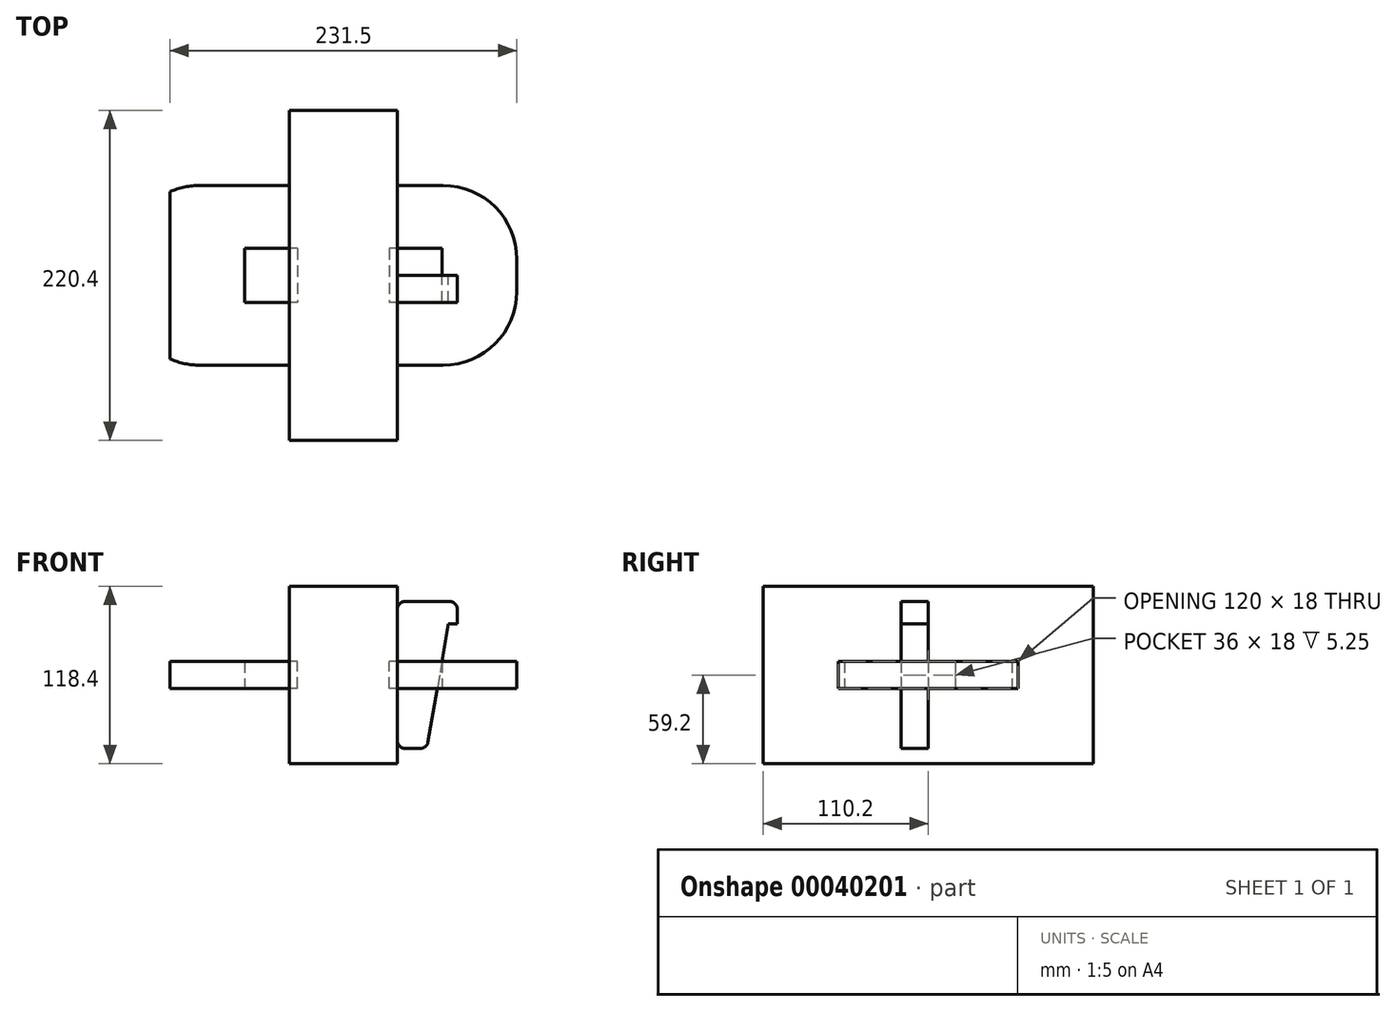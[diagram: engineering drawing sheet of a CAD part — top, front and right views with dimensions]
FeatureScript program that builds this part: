
annotation { "Feature Type Name" : "Feature", "Feature Type Description" : "" }
export const myFeature = defineFeature(function(context is Context, id is Id, definition is map)
    precondition{}
    {
        {
            var Q0;
            Q0=qCreatedBy(makeId("Top.planeOp"),FACE);
            var sketch = newSketch(context, id + "F0", { "sketchPlane" : qUnion([Q0])});
            skLineSegment(sketch, "E0.rect.bottom", {"start": v(95.75, -60) * mm, "end": v(-95.75, -60) * mm});
            skLineSegment(sketch, "E0.rect.top", {"start": v(95.75, 60) * mm, "end": v(-95.75, 60) * mm});
            skLineSegment(sketch, "E0.rect.left", {"start": v(145.75, -10) * mm, "end": v(145.75, 10) * mm});
            skLineSegment(sketch, "E0.rect.right", {"start": v(-145.75, -10) * mm, "end": v(-145.75, 10) * mm});
            skPoint(sketch, "E0.rect.middle", {"position": v(0, 0) * mm});
            skLineSegment(sketch, "E1.rect.bottom", {"start": v(65.75, -18) * mm, "end": v(-65.75, -18) * mm});
            skLineSegment(sketch, "E1.rect.top", {"start": v(65.75, 18) * mm, "end": v(-65.75, 18) * mm});
            skLineSegment(sketch, "E1.rect.left", {"start": v(65.75, -18) * mm, "end": v(65.75, 18) * mm});
            skLineSegment(sketch, "E1.rect.right", {"start": v(-65.75, -18) * mm, "end": v(-65.75, 18) * mm});
            skLineSegment(sketch, "E2", {"start": v(0, 0) * mm, "end": v(0, 60) * mm, "construction": true});
            skLineSegment(sketch, "E3", {"start": v(0, 0) * mm, "end": v(-24.77, 0) * mm, "construction": true});
            skPoint(sketch, "E4.visualSharp", {"position": v(-145.75, 60) * mm});
            skArc(sketch, "E4.filletArc", {"start": v(-95.75, 60) * mm, "mid": v(-131.1, 45.36) * mm, "end": v(-145.75, 10) * mm});
            skPoint(sketch, "E5.visualSharp", {"position": v(-145.75, -60) * mm});
            skArc(sketch, "E5.filletArc", {"start": v(-145.75, -10) * mm, "mid": v(-131.1, -45.36) * mm, "end": v(-95.75, -60) * mm});
            skPoint(sketch, "E6.visualSharp", {"position": v(145.75, 60) * mm});
            skArc(sketch, "E6.filletArc", {"start": v(145.75, 10) * mm, "mid": v(131.1, 45.36) * mm, "end": v(95.75, 60) * mm});
            skPoint(sketch, "E7.visualSharp", {"position": v(145.75, -60) * mm});
            skArc(sketch, "E7.filletArc", {"start": v(95.75, -60) * mm, "mid": v(131.1, -45.36) * mm, "end": v(145.75, -10) * mm});
            skSolve(sketch);
        }
        {
            var Q0;
            Q0=qSketchRegion(id+"F0",true);
            var Q1;
            Q1=makeQuery(id+"F0.imprint","IMPRINT",FACE,{"disambiguationData":[TD([[makeQuery(id+"F0.imprint","IMPRINT",EDGE,{"derivedFrom":sQuery(id+"F0.wireOp",EDGE,"E0.rect.bottom")}),-1.0]])]});
            extrude(context, id + "F1", {"entities" : qUnion([Q0, Q1]), "depth" : 18 * mm});
        }
        {
            var Q0;
            Q0=qCreatedBy(makeId("Right.planeOp"),FACE);
            var sketch = newSketch(context, id + "F2", { "sketchPlane" : qUnion([Q0])});
            skLineSegment(sketch, "E8.0", {"start": v(-60, 18) * mm, "end": v(-60, 0) * mm});
            skLineSegment(sketch, "E8.1", {"start": v(-60, 18) * mm, "end": v(-10, 18) * mm});
            skLineSegment(sketch, "E8.2", {"start": v(-60, 0) * mm, "end": v(-10, 0) * mm});
            skLineSegment(sketch, "E8.3", {"start": v(-10, 18) * mm, "end": v(10, 18) * mm});
            skLineSegment(sketch, "E8.4", {"start": v(10, 18) * mm, "end": v(60, 18) * mm});
            skLineSegment(sketch, "E8.5", {"start": v(10, 0) * mm, "end": v(60, 0) * mm});
            skLineSegment(sketch, "E8.6", {"start": v(-10, 0) * mm, "end": v(10, 0) * mm});
            skLineSegment(sketch, "E8.7", {"start": v(60, 18) * mm, "end": v(60, 0) * mm});
            skLineSegment(sketch, "E9.0", {"start": v(10, 68.2) * mm, "end": v(110.2, 68.2) * mm});
            skLineSegment(sketch, "E9.1", {"start": v(-10, 68.2) * mm, "end": v(10, 68.2) * mm});
            skLineSegment(sketch, "E9.2", {"start": v(-110.2, 68.2) * mm, "end": v(-10, 68.2) * mm});
            skLineSegment(sketch, "E9.3", {"start": v(-110.2, 68.2) * mm, "end": v(-110.2, -50.2) * mm});
            skLineSegment(sketch, "E9.4", {"start": v(-110.2, -50.2) * mm, "end": v(-10, -50.2) * mm});
            skLineSegment(sketch, "E9.5", {"start": v(110.2, 68.2) * mm, "end": v(110.2, -50.2) * mm});
            skLineSegment(sketch, "E9.6", {"start": v(-10, -50.2) * mm, "end": v(10, -50.2) * mm});
            skLineSegment(sketch, "E9.7", {"start": v(10, -50.2) * mm, "end": v(110.2, -50.2) * mm});
            skSolve(sketch);
        }
        {
            var Q0;
            Q0=makeQuery(id+"F2.imprint","IMPRINT",FACE,{"disambiguationData":[TD([[makeQuery(id+"F2.imprint","IMPRINT",EDGE,{"derivedFrom":sQuery(id+"F2.wireOp",EDGE,"E8.0")}),-1.0]])]});
            extrude(context, id + "F3", {"entities" : qUnion([Q0]), "endBound" : BoundingType.SYMMETRIC, "depth" : 72 * mm});
        }
        {
            var Q0;
            Q0=makeQuery(id+"F1.opExtrude","CAP_FACE",FACE,{"disambiguationData":[OSD([sQuery(id+"F0.wireOp",EDGE,"E0.rect.bottom"),sQuery(id+"F0.wireOp",EDGE,"E0.rect.top"),sQuery(id+"F0.wireOp",EDGE,"E0.rect.left"),sQuery(id+"F0.wireOp",EDGE,"E0.rect.right"),sQuery(id+"F0.wireOp",EDGE,"E1.rect.bottom"),sQuery(id+"F0.wireOp",EDGE,"E1.rect.top"),sQuery(id+"F0.wireOp",EDGE,"E1.rect.left"),sQuery(id+"F0.wireOp",EDGE,"E1.rect.right"),sQuery(id+"F0.wireOp",EDGE,"E4.filletArc"),sQuery(id+"F0.wireOp",EDGE,"E5.filletArc"),sQuery(id+"F0.wireOp",EDGE,"E6.filletArc"),sQuery(id+"F0.wireOp",EDGE,"E7.filletArc")])],"isStart":false});
            var sketch = newSketch(context, id + "F4", { "sketchPlane" : qUnion([Q0])});
            skLineSegment(sketch, "E10", {"start": v(-65.75, -18) * mm, "end": v(-30.75, -18) * mm});
            skLineSegment(sketch, "E11", {"start": v(-30.75, -18) * mm, "end": v(-30.75, 18) * mm});
            skLineSegment(sketch, "E12", {"start": v(-30.75, 18) * mm, "end": v(0, 18) * mm});
            skLineSegment(sketch, "E13", {"start": v(0, 18) * mm, "end": v(0, -18) * mm});
            skLineSegment(sketch, "E14", {"start": v(0, -18) * mm, "end": v(-30.75, -18) * mm});
            skLineSegment(sketch, "E15.MirrorCS", {"start": v(0, -18) * mm, "end": v(30.75, -18) * mm});
            skLineSegment(sketch, "E16.MirrorCS", {"start": v(30.75, -18) * mm, "end": v(30.75, 18) * mm});
            skLineSegment(sketch, "E17.MirrorCS", {"start": v(30.75, 18) * mm, "end": v(0, 18) * mm});
            skSolve(sketch);
        }
        {
            var Q0;
            Q0=qSketchRegion(id+"F4",true);
            extrude(context, id + "F5", {"entities" : qUnion([Q0]), "operationType" : NewBodyOperationType.ADD, "endBound" : BoundingType.UP_TO_NEXT, "oppositeDirection" : true, "depth" : 25 * mm});
        }
        {
            var Q0;
            Q0=makeQuery(id+"F5.boolean.opBoolean","MERGE",FACE,{"derivedFrom":[makeQuery(id+"F1.opExtrude","CAP_FACE",FACE,{"disambiguationData":[OSD([sQuery(id+"F0.wireOp",EDGE,"E0.rect.bottom"),sQuery(id+"F0.wireOp",EDGE,"E0.rect.top"),sQuery(id+"F0.wireOp",EDGE,"E0.rect.left"),sQuery(id+"F0.wireOp",EDGE,"E0.rect.right"),sQuery(id+"F0.wireOp",EDGE,"E1.rect.bottom"),sQuery(id+"F0.wireOp",EDGE,"E1.rect.top"),sQuery(id+"F0.wireOp",EDGE,"E1.rect.left"),sQuery(id+"F0.wireOp",EDGE,"E1.rect.right"),sQuery(id+"F0.wireOp",EDGE,"E4.filletArc"),sQuery(id+"F0.wireOp",EDGE,"E5.filletArc"),sQuery(id+"F0.wireOp",EDGE,"E6.filletArc"),sQuery(id+"F0.wireOp",EDGE,"E7.filletArc")])],"isStart":false}),makeQuery(id+"F5.opExtrude","CAP_FACE",FACE,{"disambiguationData":[OSD([sQuery(id+"F4.wireOp",EDGE,"E11"),sQuery(id+"F4.wireOp",EDGE,"E12"),sQuery(id+"F4.wireOp",EDGE,"E14"),sQuery(id+"F4.wireOp",EDGE,"E15.MirrorCS"),sQuery(id+"F4.wireOp",EDGE,"E16.MirrorCS"),sQuery(id+"F4.wireOp",EDGE,"E17.MirrorCS")])],"isStart":true})]});
            var sketch = newSketch(context, id + "F6", { "sketchPlane" : qUnion([Q0])});
            skLineSegment(sketch, "E18.rect.bottom", {"start": v(-115.75, -60) * mm, "end": v(115.75, -60) * mm});
            skLineSegment(sketch, "E18.rect.top", {"start": v(-115.75, 60) * mm, "end": v(115.75, 60) * mm});
            skLineSegment(sketch, "E18.rect.left", {"start": v(-115.75, -60) * mm, "end": v(-115.75, 60) * mm});
            skLineSegment(sketch, "E18.rect.right", {"start": v(115.75, -60) * mm, "end": v(115.75, 60) * mm});
            skPoint(sketch, "E18.rect.middle", {"position": v(0, 0) * mm});
            skLineSegment(sketch, "E19", {"start": v(-115.75, 60) * mm, "end": v(-171.14, 60) * mm});
            skLineSegment(sketch, "E20", {"start": v(-171.14, 60) * mm, "end": v(-171.14, -60) * mm});
            skLineSegment(sketch, "E21", {"start": v(-171.14, -60) * mm, "end": v(-115.75, -60) * mm});
            skLineSegment(sketch, "E22", {"start": v(115.75, -60) * mm, "end": v(180.93, -60) * mm});
            skLineSegment(sketch, "E23", {"start": v(180.93, -60) * mm, "end": v(180.93, 60) * mm});
            skLineSegment(sketch, "E24", {"start": v(180.93, 60) * mm, "end": v(115.75, 60) * mm});
            skSolve(sketch);
        }
        {
            var Q0;
            {var subQ7=sQuery(id+"F6.wireOp",EDGE,"E19");Q0=makeQuery(id+"F6.imprint","IMPRINT",FACE,{"disambiguationData":[TD([[makeQuery(id+"F6.imprint","IMPRINT",EDGE,{"derivedFrom":subQ7}),1.0]])]});}
            var Q1;
            {var subQ7=sQuery(id+"F6.wireOp",EDGE,"E22");Q1=makeQuery(id+"F6.imprint","IMPRINT",FACE,{"disambiguationData":[TD([[makeQuery(id+"F6.imprint","IMPRINT",EDGE,{"derivedFrom":subQ7}),1.0]])]});}
            var Q2;
            {var subQ3=makeQuery(id+"F1.opExtrude","CAP_EDGE",EDGE,{"disambiguationData":[OSD([sQuery(id+"F0.wireOp",EDGE,"E0.rect.right")])],"isStart":false});Q2=makeQuery(id+"F6.imprint","IMPRINT",FACE,{"disambiguationData":[TD([[makeQuery(id+"F6.imprint","IMPRINT",EDGE,{"derivedFrom":subQ3}),-1.0]])]});}
            var Q3;
            {var subQ3=makeQuery(id+"F1.opExtrude","CAP_EDGE",EDGE,{"disambiguationData":[OSD([sQuery(id+"F0.wireOp",EDGE,"E0.rect.left")])],"isStart":false});Q3=makeQuery(id+"F6.imprint","IMPRINT",FACE,{"disambiguationData":[TD([[makeQuery(id+"F6.imprint","IMPRINT",EDGE,{"derivedFrom":subQ3}),1.0]])]});}
            extrude(context, id + "F7", {"entities" : qUnion([Q0, Q1, Q2, Q3]), "operationType" : NewBodyOperationType.REMOVE, "oppositeDirection" : true, "depth" : 25 * mm});
        }
        {
            var Q0;
            {var subQ0=makeQuery(id+"F1.opExtrude","CAP_EDGE",EDGE,{"disambiguationData":[OSD([sQuery(id+"F0.wireOp",EDGE,"E4.filletArc")])],"isStart":false});var subQ3=sQuery(id+"F6.wireOp",EDGE,"E18.rect.top");var subQ4=makeQuery(id+"F6.imprint","INTERSECT",VERTEX,{"derivedFrom":[subQ0,subQ3]});Q0=makeQuery(id+"F6.imprint","IMPRINT",FACE,{"disambiguationData":[TD([[makeQuery(id+"F6.imprint","IMPRINT",EDGE,{"disambiguationData":[TD([[subQ4,-1.0]])],"derivedFrom":subQ0}),-1.0]])]});}
            var Q1;
            {var subQ0=makeQuery(id+"F1.opExtrude","CAP_EDGE",EDGE,{"disambiguationData":[OSD([sQuery(id+"F0.wireOp",EDGE,"E6.filletArc")])],"isStart":false});var subQ3=sQuery(id+"F6.wireOp",EDGE,"E18.rect.top");var subQ4=makeQuery(id+"F6.imprint","INTERSECT",VERTEX,{"derivedFrom":[subQ0,subQ3]});Q1=makeQuery(id+"F6.imprint","IMPRINT",FACE,{"disambiguationData":[TD([[makeQuery(id+"F6.imprint","IMPRINT",EDGE,{"disambiguationData":[TD([[subQ4,1.0]])],"derivedFrom":subQ0}),-1.0]])]});}
            var Q2;
            {var subQ0=makeQuery(id+"F1.opExtrude","CAP_EDGE",EDGE,{"disambiguationData":[OSD([sQuery(id+"F0.wireOp",EDGE,"E7.filletArc")])],"isStart":false});var subQ3=sQuery(id+"F6.wireOp",EDGE,"E18.rect.bottom");var subQ4=makeQuery(id+"F6.imprint","INTERSECT",VERTEX,{"derivedFrom":[subQ0,subQ3]});Q2=makeQuery(id+"F6.imprint","IMPRINT",FACE,{"disambiguationData":[TD([[makeQuery(id+"F6.imprint","IMPRINT",EDGE,{"disambiguationData":[TD([[subQ4,-1.0]])],"derivedFrom":subQ0}),-1.0]])]});}
            var Q3;
            {var subQ0=makeQuery(id+"F1.opExtrude","CAP_EDGE",EDGE,{"disambiguationData":[OSD([sQuery(id+"F0.wireOp",EDGE,"E5.filletArc")])],"isStart":false});var subQ3=sQuery(id+"F6.wireOp",EDGE,"E18.rect.bottom");var subQ4=makeQuery(id+"F6.imprint","INTERSECT",VERTEX,{"derivedFrom":[subQ0,subQ3]});Q3=makeQuery(id+"F6.imprint","IMPRINT",FACE,{"disambiguationData":[TD([[makeQuery(id+"F6.imprint","IMPRINT",EDGE,{"disambiguationData":[TD([[subQ4,1.0]])],"derivedFrom":subQ0}),-1.0]])]});}
            extrude(context, id + "F8", {"entities" : qUnion([Q0, Q1, Q2, Q3]), "operationType" : NewBodyOperationType.ADD, "oppositeDirection" : true, "depth" : 18 * mm});
        }
        {
            var Q0;
            Q0=makeQuery(id+"F8.opExtrude","SWEPT_EDGE",EDGE,{"disambiguationData":[OSD([sQuery(id+"F6.wireOp",EDGE,"E18.rect.top"),sQuery(id+"F6.wireOp",EDGE,"E18.rect.left"),sQuery(id+"F6.wireOp",EDGE,"E19")])]});
            var Q1;
            Q1=makeQuery(id+"F8.opExtrude","SWEPT_EDGE",EDGE,{"disambiguationData":[OSD([sQuery(id+"F6.wireOp",EDGE,"E18.rect.bottom"),sQuery(id+"F6.wireOp",EDGE,"E18.rect.left"),sQuery(id+"F6.wireOp",EDGE,"E21")])]});
            var Q2;
            Q2=makeQuery(id+"F8.opExtrude","SWEPT_EDGE",EDGE,{"disambiguationData":[OSD([sQuery(id+"F6.wireOp",EDGE,"E18.rect.bottom"),sQuery(id+"F6.wireOp",EDGE,"E18.rect.right"),sQuery(id+"F6.wireOp",EDGE,"E22")])]});
            var Q3;
            Q3=makeQuery(id+"F8.opExtrude","SWEPT_EDGE",EDGE,{"disambiguationData":[OSD([sQuery(id+"F6.wireOp",EDGE,"E18.rect.top"),sQuery(id+"F6.wireOp",EDGE,"E18.rect.right"),sQuery(id+"F6.wireOp",EDGE,"E24")])]});
            fillet(context, id + "F9", {"entities" : qUnion([Q0, Q1, Q2, Q3]), "radius" : 49.23 * mm, "tangentPropagation" : true, "allowEdgeOverflow" : false});
        }
        {
            var Q0;
            Q0=qCreatedBy(makeId("Front.planeOp"),FACE);
            var sketch = newSketch(context, id + "F10", { "sketchPlane" : qUnion([Q0])});
            skLineSegment(sketch, "E25.0", {"start": v(36, 68.2) * mm, "end": v(36, -50.2) * mm});
            skLineSegment(sketch, "E26.1", {"start": v(65.75, 18) * mm, "end": v(65.75, 0) * mm});
            skLineSegment(sketch, "E27.0", {"start": v(66.52, 18) * mm, "end": v(-66.52, 18) * mm, "construction": true});
            skLineSegment(sketch, "E28", {"start": v(36, 18) * mm, "end": v(36, 53) * mm});
            skLineSegment(sketch, "E29.0", {"start": v(66.52, 0) * mm, "end": v(-66.52, 0) * mm, "construction": true});
            skLineSegment(sketch, "E30", {"start": v(36, 18) * mm, "end": v(36, 0) * mm});
            skLineSegment(sketch, "E31", {"start": v(36, 0) * mm, "end": v(36, -40) * mm});
            skLineSegment(sketch, "E32", {"start": v(41, 58) * mm, "end": v(71, 58) * mm});
            skLineSegment(sketch, "E33", {"start": v(65.75, 0) * mm, "end": v(65.75, -41.28) * mm, "construction": true});
            skLineSegment(sketch, "E34", {"start": v(41, -40) * mm, "end": v(51.54, -40) * mm});
            skLineSegment(sketch, "E35", {"start": v(36, -35) * mm, "end": v(36, -30) * mm});
            skLineSegment(sketch, "E36", {"start": v(36, 18) * mm, "end": v(65.75, 18) * mm});
            skLineSegment(sketch, "E37", {"start": v(65.75, 18) * mm, "end": v(56.47, -35.85) * mm});
            skLineSegment(sketch, "E38", {"start": v(65.75, 18) * mm, "end": v(70.06, 43) * mm});
            skLineSegment(sketch, "E39", {"start": v(36, 18) * mm, "end": v(36, 43) * mm});
            skLineSegment(sketch, "E40", {"start": v(36, 43) * mm, "end": v(98.36, 43) * mm, "construction": true});
            skLineSegment(sketch, "E41", {"start": v(70.06, 43) * mm, "end": v(76, 43) * mm});
            skLineSegment(sketch, "E42", {"start": v(76, 43) * mm, "end": v(76, 53) * mm});
            skPoint(sketch, "E43.visualSharp", {"position": v(76, 58) * mm});
            skArc(sketch, "E43.filletArc", {"start": v(76, 53) * mm, "mid": v(74.54, 56.54) * mm, "end": v(71, 58) * mm});
            skPoint(sketch, "E44.visualSharp", {"position": v(36, 58) * mm});
            skArc(sketch, "E44.filletArc", {"start": v(41, 58) * mm, "mid": v(37.46, 56.54) * mm, "end": v(36, 53) * mm});
            skPoint(sketch, "E45.visualSharp", {"position": v(36, -40) * mm});
            skArc(sketch, "E45.filletArc", {"start": v(36, -35) * mm, "mid": v(37.46, -38.54) * mm, "end": v(41, -40) * mm});
            skPoint(sketch, "E46.visualSharp", {"position": v(55.75, -40) * mm});
            skArc(sketch, "E46.filletArc", {"start": v(51.54, -40) * mm, "mid": v(54.76, -38.82) * mm, "end": v(56.47, -35.85) * mm});
            skSolve(sketch);
        }
        {
            var Q0;
            Q0=qSketchRegion(id+"F10",true);
            extrude(context, id + "F11", {"entities" : qUnion([Q0]), "depth" : 18 * mm});
        }
    });
